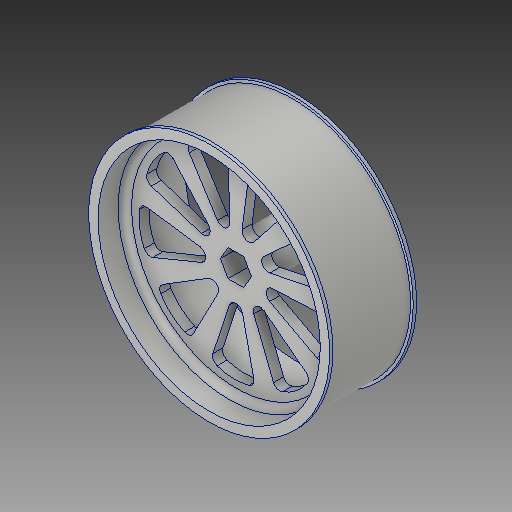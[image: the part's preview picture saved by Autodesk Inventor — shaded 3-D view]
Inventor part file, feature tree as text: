
AUTODESK INVENTOR PART (.ipt)
format: ipt  version: 2019.4 (Build 234330000, 330)  size: 798,720 bytes
history: native  units: in
note: dims shown in document units (in); Inventor stores cm internally (conversion verified against a paired STEP export)
features: extrude x7, fillet x7, sketch x7, pattern_circular x2, chamfer x2, plane x1, mirror x1, projected_geometry x1
ambient origin geometry x8: Origin, YZ Plane, XZ Plane, XY Plane, X Axis, Y Axis, Z Axis, Center Point
bodies: Solid1 (feature_tree)
feature tree (28):
  extrude  "Extrusion1"  Depth=0.75in
  extrude  "Extrusion4"  Depth=0.125in
  extrude  "Extrusion5"  Depth=0.5in TaperAngle=0.0deg
  extrude  "Extrusion6"  Depth=0.125in TaperAngle=0.0deg
  extrude  "Extrusion8"  Depth=0.1875in
  fillet  "Fillet1"  Radius=0.1875in
  pattern_circular  "Circular Pattern1"  [2 undecoded]
  fillet  "Fillet2"  Radius=0.938in
  extrude  "Extrusion9"  Depth=0.125in
  plane  "Work Plane1"
  mirror  "Mirror1"
  fillet  "Fillet3"  Radius=3.5433in
  fillet  "Fillet4"  Radius=0.13in
  fillet  "Fillet5"  Radius=4.5in
  extrude  "Extrusion10"  Depth=0.0625in TaperAngle=0.0deg
  pattern_circular  "Circular Pattern2"  [2 undecoded]
  fillet  "Fillet7"  Radius=0.125in
  fillet  "Fillet8"  Radius=0.125in
  chamfer  "Chamfer1"  Distance=0.125in
  chamfer  "Chamfer2"  Distance=0.125in
  sketch  "Sketch1"  dims[d0=4.4in d1=0.75in]
  sketch  "Sketch4"  dims[d2=0.504in d3=0.125in]
  sketch  "Sketch5"  dims[d9=1.625in d10=0.0in d24=0.5in d25=0.0in]
  sketch  "Sketch6"  dims[d26=0.75in d27=0.125in d28=0.0in]
  sketch  "Sketch7"  dims[d30=0.938in d31=0.0in d41=0.1875in d42=0.1875in]
  sketch  "Sketch8"  dims[d43=1.3568in]
  sketch  "Sketch9"  dims[d44=1.4375in d45=0.1875in d46=0.938in d47=0.0in d48=0.13in d49=3.5433in d50=360.0deg d52=0.13in d53=4.5in d54=0.0625in d55=0.0in d56=0.125in d57=0.125in d58=0.125in d59=0.125in d60=0.125in d62=0.2in d63=0.25in d70=1.0in d71=0.0in d72=3.5433in d73=360.0deg d77=1.0in d78=1.0in d79=0.25in d80=0.25in d81=0.5241in d82=0.947in d83=1.6614in d84=1.0272in d85=0.7in d87=0.015in d88=0.015in d89=0.0156in d90=0.125in d91=45.0deg d92=0.0156in d93=0.125in d94=45.0deg]
  projected_geometry  "Projected Loop1"
note: 4 required parameter values undecoded (feature->parameter linkage not recoverable at this tier; creation-order binding heuristic only, values carry confidence <= 0.55)
